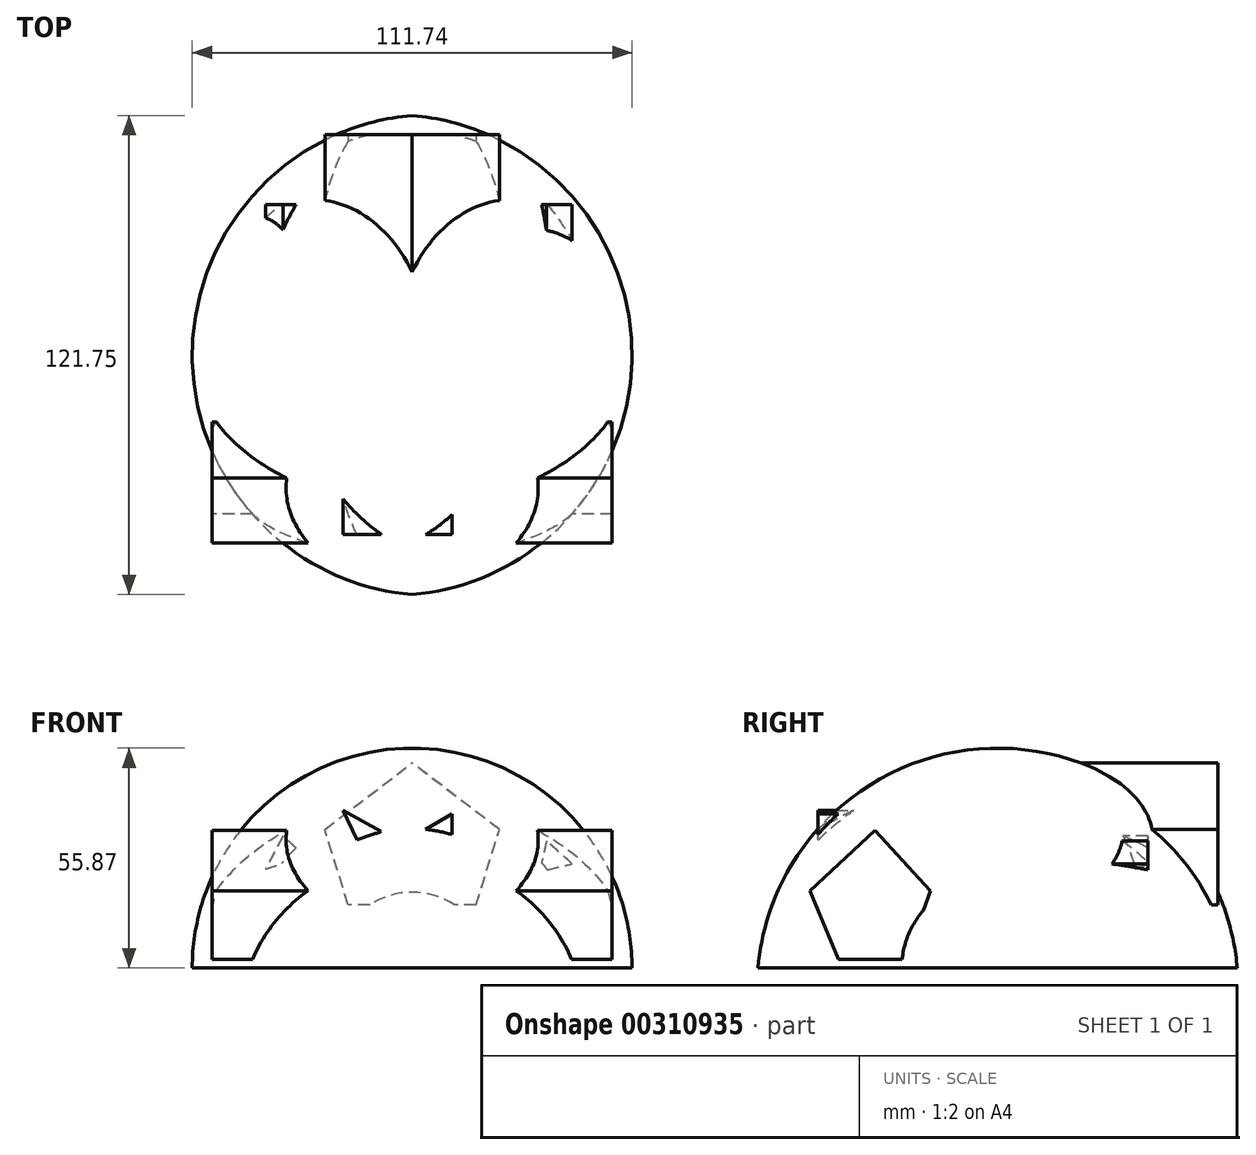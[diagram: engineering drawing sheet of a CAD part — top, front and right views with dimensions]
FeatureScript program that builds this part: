
annotation { "Feature Type Name" : "Feature", "Feature Type Description" : "" }
export const myFeature = defineFeature(function(context is Context, id is Id, definition is map)
    precondition{}
    {
        {
            var Q0;
            Q0=qCreatedBy(makeId("Right.planeOp"),FACE);
            var sketch = newSketch(context, id + "F0", { "sketchPlane" : qUnion([Q0])});
            skLineSegment(sketch, "E0", {"start": v(-68.59, -10.65) * mm, "end": v(53.16, -10.65) * mm});
            skArc(sketch, "E1", {"start": v(53.16, -10.65) * mm, "mid": v(-7.71, 45.22) * mm, "end": v(-68.59, -10.65) * mm});
            skSolve(sketch);
        }
        {
            var Q0;
            Q0=makeQuery(id+"F0.imprint","IMPRINT",FACE,{"disambiguationData":[TD([[makeQuery(id+"F0.imprint","IMPRINT",EDGE,{"derivedFrom":sQuery(id+"F0.wireOp",EDGE,"E0")}),1.0]])]});
            var Q1;
            Q1=sQuery(id+"F0.wireOp",EDGE,"E0");
            revolve(context, id + "F1", {"entities" : qUnion([Q0]), "axis" : qUnion([Q1]), "revolveType" : RevolveType.TWO_DIRECTIONS, "angle" : 90 * degree, "angleBack" : 270 * degree});
        }
        {
            var Q0;
            Q0=qCreatedBy(makeId("Right.planeOp"),FACE);
            var sketch = newSketch(context, id + "F2", { "sketchPlane" : qUnion([Q0])});
            skLineSegment(sketch, "E2", {"start": v(-48.12, -8.42) * mm, "end": v(-55.42, 9.01) * mm});
            skLineSegment(sketch, "E3", {"start": v(-55.42, 9.01) * mm, "end": v(-38.93, 24.28) * mm});
            skLineSegment(sketch, "E4", {"start": v(-38.93, 24.28) * mm, "end": v(-24.79, 9.01) * mm});
            skLineSegment(sketch, "E5", {"start": v(-24.79, 9.01) * mm, "end": v(-31.1, -8.42) * mm});
            skLineSegment(sketch, "E6", {"start": v(-31.1, -8.42) * mm, "end": v(-48.12, -8.42) * mm});
            skSolve(sketch);
        }
        {
            var Q0;
            Q0 = qSketchRegion(id + "F2", true);
            extrude(context, id + "F3", {"entities" : qUnion([Q0]), "operationType" : NewBodyOperationType.ADD, "endBound" : BoundingType.SYMMETRIC, "depth" : 101.6 * mm});
        }
        {
            var Q0;
            Q0=qCreatedBy(makeId("Front.planeOp"),FACE);
            var sketch = newSketch(context, id + "F4", { "sketchPlane" : qUnion([Q0])});
            skLineSegment(sketch, "E7", {"start": v(11.4, 5.35) * mm, "end": v(-16.23, 5.35) * mm});
            skLineSegment(sketch, "E8", {"start": v(-16.23, 5.35) * mm, "end": v(-22.17, 24.54) * mm});
            skLineSegment(sketch, "E9", {"start": v(-22.17, 24.54) * mm, "end": v(0, 41.44) * mm});
            skLineSegment(sketch, "E10.MirrorCS", {"start": v(22.17, 24.54) * mm, "end": v(0, 41.44) * mm});
            skLineSegment(sketch, "E11.MirrorCS", {"start": v(16.23, 5.35) * mm, "end": v(22.17, 24.54) * mm});
            skLineSegment(sketch, "E12.MirrorCS", {"start": v(-11.4, 5.35) * mm, "end": v(16.23, 5.35) * mm});
            skSolve(sketch);
        }
        {
            var Q0;
            Q0 = qSketchRegion(id + "F4", true);
            extrude(context, id + "F5", {"entities" : qUnion([Q0]), "operationType" : NewBodyOperationType.ADD, "oppositeDirection" : true, "depth" : 48.26 * mm});
        }
        {
            var Q0;
            Q0=qCreatedBy(makeId("Front.planeOp"),FACE);
            var sketch = newSketch(context, id + "F6", { "sketchPlane" : qUnion([Q0])});
            skLineSegment(sketch, "E13", {"start": v(-12.87, 19.3) * mm, "end": v(-17.51, 29.42) * mm});
            skLineSegment(sketch, "E14", {"start": v(-17.51, 29.42) * mm, "end": v(-7.95, 24.07) * mm});
            skLineSegment(sketch, "E15", {"start": v(-7.95, 24.07) * mm, "end": v(-12.87, 19.3) * mm});
            skLineSegment(sketch, "E16", {"start": v(-8.93, 11.7) * mm, "end": v(-12.73, 2.13) * mm});
            skLineSegment(sketch, "E17", {"start": v(-12.73, 2.13) * mm, "end": v(-1.33, 5.08) * mm});
            skLineSegment(sketch, "E18", {"start": v(-1.33, 5.08) * mm, "end": v(-8.93, 11.7) * mm});
            skLineSegment(sketch, "E19", {"start": v(1.62, 23.51) * mm, "end": v(10.2, 28.58) * mm});
            skLineSegment(sketch, "E20", {"start": v(10.2, 28.58) * mm, "end": v(10.2, 19.85) * mm});
            skLineSegment(sketch, "E21", {"start": v(10.2, 19.85) * mm, "end": v(1.62, 23.51) * mm});
            skSolve(sketch);
        }
        {
            var Q0;
            Q0 = qSketchRegion(id + "F6", true);
            extrude(context, id + "F7", {"entities" : qUnion([Q0]), "operationType" : NewBodyOperationType.ADD, "depth" : 53.34 * mm});
        }
        {
            var Q0;
            Q0=qCreatedBy(makeId("Front.planeOp"),FACE);
            var sketch = newSketch(context, id + "F8", { "sketchPlane" : qUnion([Q0])});
            skLineSegment(sketch, "E22", {"start": v(40.65, 15.8) * mm, "end": v(34.15, 21.7) * mm});
            skLineSegment(sketch, "E23", {"start": v(34.15, 21.7) * mm, "end": v(32.36, 13.84) * mm});
            skLineSegment(sketch, "E24", {"start": v(32.36, 13.84) * mm, "end": v(40.65, 15.8) * mm});
            skLineSegment(sketch, "E25", {"start": v(-27.2, 17.77) * mm, "end": v(-32.83, 22.88) * mm});
            skPoint(sketch, "E25.startSnap0", {"position": v(33.25, 17.77) * mm});
            skLineSegment(sketch, "E26", {"start": v(-32.83, 22.88) * mm, "end": v(-37.26, 14.5) * mm});
            skLineSegment(sketch, "E27", {"start": v(-37.26, 14.5) * mm, "end": v(-27.2, 17.77) * mm});
            skSolve(sketch);
        }
        {
            var Q0;
            Q0 = qSketchRegion(id + "F8", true);
            extrude(context, id + "F9", {"entities" : qUnion([Q0]), "operationType" : NewBodyOperationType.ADD, "oppositeDirection" : true, "depth" : 30.48 * mm});
        }
    });
